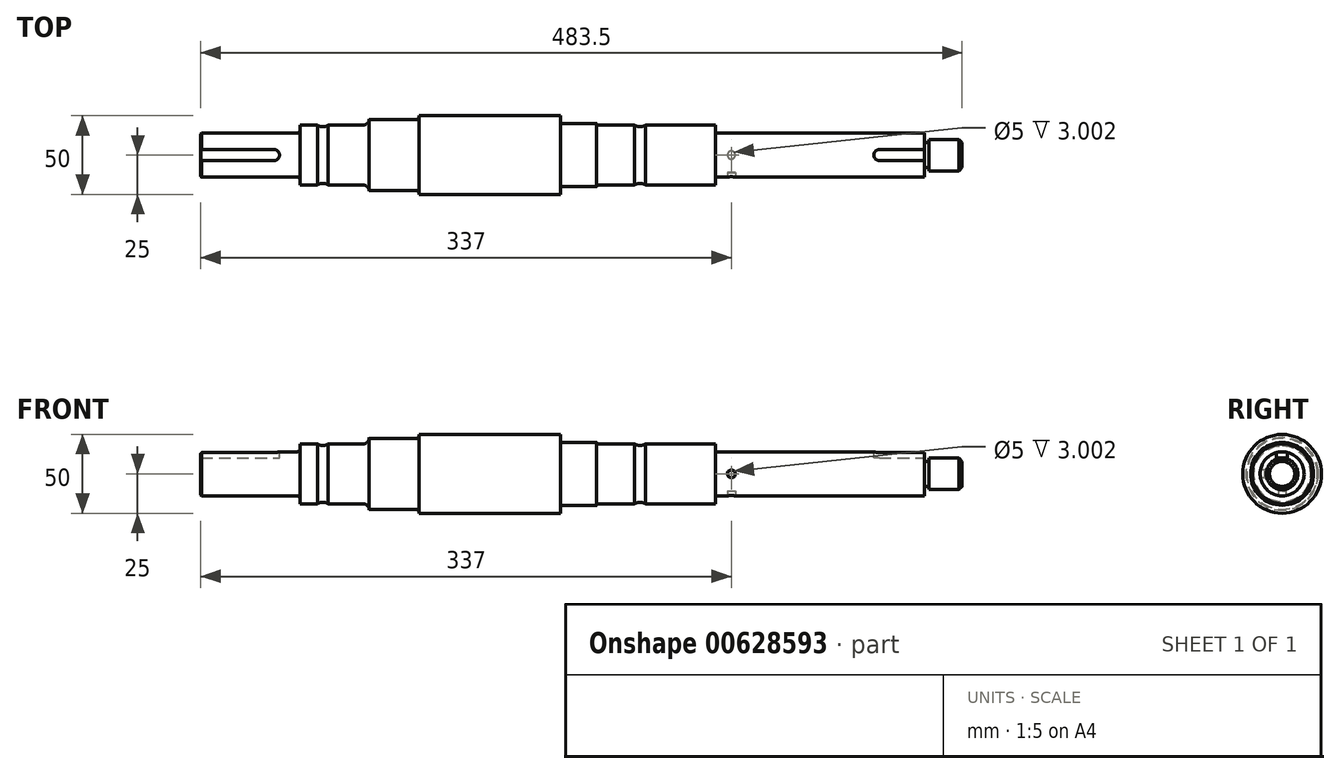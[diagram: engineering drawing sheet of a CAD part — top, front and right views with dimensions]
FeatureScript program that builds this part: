
annotation { "Feature Type Name" : "Feature", "Feature Type Description" : "" }
export const myFeature = defineFeature(function(context is Context, id is Id, definition is map)
    precondition{}
    {
        {
            var Q0;
            Q0=qCreatedBy(makeId("Front.planeOp"),FACE);
            var sketch = newSketch(context, id + "F0", { "sketchPlane" : qUnion([Q0])});
            skLineSegment(sketch, "E0", {"start": v(0, 0) * mm, "end": v(0, 14) * mm});
            skLineSegment(sketch, "E1", {"start": v(0, 14) * mm, "end": v(61, 14) * mm});
            skLineSegment(sketch, "E2", {"start": v(63, 16) * mm, "end": v(63, 19) * mm});
            skLineSegment(sketch, "E3", {"start": v(63, 19) * mm, "end": v(74.1, 19) * mm});
            skArc(sketch, "E4", {"start": v(74.1, 19) * mm, "mid": v(77.5, 18) * mm, "end": v(80.9, 19) * mm});
            skLineSegment(sketch, "E5", {"start": v(80.9, 19) * mm, "end": v(103, 19) * mm});
            skLineSegment(sketch, "E6", {"start": v(107, 22.5) * mm, "end": v(107, 23) * mm});
            skLineSegment(sketch, "E7", {"start": v(107, 22.5) * mm, "end": v(137, 22.5) * mm});
            skLineSegment(sketch, "E8", {"start": v(138.5, 24) * mm, "end": v(138.5, 25) * mm});
            skLineSegment(sketch, "E9", {"start": v(138.5, 25) * mm, "end": v(228.5, 25) * mm});
            skLineSegment(sketch, "E10", {"start": v(228.5, 25) * mm, "end": v(228.5, 21.5) * mm});
            skLineSegment(sketch, "E11", {"start": v(230, 20) * mm, "end": v(251.5, 20) * mm});
            skLineSegment(sketch, "E12", {"start": v(252.91, 19) * mm, "end": v(275.6, 19) * mm});
            skArc(sketch, "E13", {"start": v(275.6, 19) * mm, "mid": v(279, 18) * mm, "end": v(282.4, 19) * mm});
            skLineSegment(sketch, "E14", {"start": v(282.4, 19) * mm, "end": v(327, 19) * mm});
            skLineSegment(sketch, "E15", {"start": v(327, 19) * mm, "end": v(327, 15.5) * mm});
            skLineSegment(sketch, "E16", {"start": v(328.5, 14) * mm, "end": v(459.5, 14) * mm});
            skLineSegment(sketch, "E17", {"start": v(459.5, 14) * mm, "end": v(459.5, 8) * mm});
            skLineSegment(sketch, "E18", {"start": v(459.5, 8) * mm, "end": v(462.5, 8) * mm});
            skLineSegment(sketch, "E19", {"start": v(462.5, 8) * mm, "end": v(462.5, 10) * mm});
            skLineSegment(sketch, "E20", {"start": v(462.5, 10) * mm, "end": v(483.5, 10) * mm});
            skLineSegment(sketch, "E21", {"start": v(483.5, 10) * mm, "end": v(483.5, 0) * mm});
            skLineSegment(sketch, "E22", {"start": v(0, 0) * mm, "end": v(548.97, 0) * mm, "construction": true});
            skPoint(sketch, "E23", {"position": v(77.5, 18) * mm});
            skPoint(sketch, "E24", {"position": v(279, 18) * mm});
            skLineSegment(sketch, "E25", {"start": v(0, 0) * mm, "end": v(483.5, 0) * mm});
            skPoint(sketch, "E26.visualSharp", {"position": v(63, 14) * mm});
            skArc(sketch, "E26.filletArc", {"start": v(61, 14) * mm, "mid": v(62.41, 14.59) * mm, "end": v(63, 16) * mm});
            skPoint(sketch, "E27.visualSharp", {"position": v(107, 19) * mm});
            skArc(sketch, "E27.filletArc", {"start": v(103, 19) * mm, "mid": v(105.83, 20.17) * mm, "end": v(107, 23) * mm});
            skPoint(sketch, "E28.visualSharp", {"position": v(138.5, 22.5) * mm});
            skArc(sketch, "E28.filletArc", {"start": v(137, 22.5) * mm, "mid": v(138.06, 22.94) * mm, "end": v(138.5, 24) * mm});
            skPoint(sketch, "E29.visualSharp", {"position": v(228.5, 20) * mm});
            skArc(sketch, "E29.filletArc", {"start": v(228.5, 21.5) * mm, "mid": v(228.94, 20.44) * mm, "end": v(230, 20) * mm});
            skPoint(sketch, "E30.visualSharp", {"position": v(251.5, 19) * mm});
            skPoint(sketch, "E31.visualSharp", {"position": v(327, 14) * mm});
            skArc(sketch, "E31.filletArc", {"start": v(327, 15.5) * mm, "mid": v(327.44, 14.44) * mm, "end": v(328.5, 14) * mm});
            skArc(sketch, "E32", {"start": v(251.5, 20) * mm, "mid": v(252.05, 19.28) * mm, "end": v(252.91, 19) * mm});
            skSolve(sketch);
        }
        {
            var Q0;
            Q0 = qSketchRegion(id + "F0", true);
            var Q1;
            Q1=sQuery(id+"F0.wireOp",EDGE,"E22");
            revolve(context, id + "F1", {"surfaceOperationType" : NewSurfaceOperationType.NEW, "entities" : qUnion([Q0]), "axis" : qUnion([Q1]), "revolveType" : RevolveType.FULL});
        }
        {
            var Q0;
            Q0=makeQuery(id+"F1.opRevolve","SWEPT_EDGE",EDGE,{"disambiguationData":[OSD([sQuery(id+"F0.wireOp",EDGE,"E0"),sQuery(id+"F0.wireOp",EDGE,"E1")])]});
            chamfer(context, id + "F2", {"entities" : qUnion([Q0]), "chamferType" : ChamferType.OFFSET_ANGLE, "width" : 0.5 * mm, "oppositeDirection" : false, "angle" : 45 * degree, "tangentPropagation" : true});
        }
        {
            var Q0;
            Q0=makeQuery(id+"F1.opRevolve","SWEPT_EDGE",EDGE,{"disambiguationData":[OSD([sQuery(id+"F0.wireOp",EDGE,"E20"),sQuery(id+"F0.wireOp",EDGE,"E21")])]});
            chamfer(context, id + "F3", {"entities" : qUnion([Q0]), "chamferType" : ChamferType.OFFSET_ANGLE, "width" : 2 * mm, "oppositeDirection" : false, "angle" : 45 * degree, "tangentPropagation" : true});
        }
        {
            var Q0;
            Q0=qCreatedBy(makeId("Top.planeOp"),FACE);
            cPlane(context, id + "F4", {"entities" : qUnion([Q0]), "cplaneType" : CPlaneType.OFFSET, "offset" : 14 * mm, "width" : 150 * mm, "height" : 150 * mm});
        }
        {
            var Q0;
            Q0=qCreatedBy(id+"F4.planeOp",FACE);
            var sketch = newSketch(context, id + "F5", { "sketchPlane" : qUnion([Q0])});
            skArc(sketch, "E33", {"start": v(46.5, -3.5) * mm, "mid": v(50, 0) * mm, "end": v(46.5, 3.5) * mm});
            skLineSegment(sketch, "E34", {"start": v(0, 0) * mm, "end": v(53.71, 0) * mm, "construction": true});
            skLineSegment(sketch, "E35.0", {"start": v(0, -3.5) * mm, "end": v(46.5, -3.5) * mm});
            skLineSegment(sketch, "E36.MirrorCS", {"start": v(0, 3.5) * mm, "end": v(46.5, 3.5) * mm});
            skPoint(sketch, "E37", {"position": v(50, 0) * mm});
            skLineSegment(sketch, "E38", {"start": v(0, 3.5) * mm, "end": v(0, -3.5) * mm});
            skSolve(sketch);
        }
        {
            var Q0;
            Q0 = qSketchRegion(id + "F5", true);
            extrude(context, id + "F6", {"entities" : qUnion([Q0]), "operationType" : NewBodyOperationType.REMOVE, "oppositeDirection" : true, "depth" : 4 * mm, "offsetDistance" : 25 * mm});
        }
        {
            var Q0;
            Q0=qCreatedBy(id+"F4.planeOp",FACE);
            var sketch = newSketch(context, id + "F7", { "sketchPlane" : qUnion([Q0])});
            skLineSegment(sketch, "E39", {"start": v(0, 0) * mm, "end": v(507.23, 0) * mm, "construction": true});
            skArc(sketch, "E40", {"start": v(431, 3.5) * mm, "mid": v(427.5, 0) * mm, "end": v(431, -3.5) * mm});
            skLineSegment(sketch, "E41", {"start": v(431, 3.5) * mm, "end": v(459.5, 3.5) * mm});
            skLineSegment(sketch, "E42", {"start": v(431, -3.5) * mm, "end": v(459.5, -3.5) * mm});
            skLineSegment(sketch, "E43.0", {"start": v(459.5, -3.5) * mm, "end": v(459.5, 3.5) * mm});
            skPoint(sketch, "E44.orphan", {"position": v(459.5, 14) * mm});
            skPoint(sketch, "E45.orphan", {"position": v(459.5, -14) * mm});
            skPoint(sketch, "E46", {"position": v(427.5, 0) * mm});
            skSolve(sketch);
        }
        {
            var Q0;
            Q0 = qSketchRegion(id + "F7", true);
            extrude(context, id + "F8", {"entities" : qUnion([Q0]), "operationType" : NewBodyOperationType.REMOVE, "oppositeDirection" : true, "depth" : 4 * mm, "offsetDistance" : 25 * mm});
        }
        {
            var Q0;
            Q0=qCreatedBy(makeId("Front.planeOp"),FACE);
            cPlane(context, id + "F9", {"entities" : qUnion([Q0]), "cplaneType" : CPlaneType.OFFSET, "offset" : 14 * mm, "width" : 150 * mm, "height" : 150 * mm});
        }
        {
            var Q0;
            Q0=qCreatedBy(id+"F9.planeOp",FACE);
            var sketch = newSketch(context, id + "F10", { "sketchPlane" : qUnion([Q0])});
            skLineSegment(sketch, "E47", {"start": v(0, 0) * mm, "end": v(497.27, 0) * mm, "construction": true});
            skCircle(sketch, "E48", {"center": v(337, 0) * mm, "radius": 2.5 * mm});
            skSolve(sketch);
        }
        {
            var Q0;
            Q0 = qSketchRegion(id + "F10", true);
            extrude(context, id + "F11", {"entities" : qUnion([Q0]), "operationType" : NewBodyOperationType.REMOVE, "oppositeDirection" : true, "depth" : 3 * mm, "offsetDistance" : 25 * mm});
        }
        {
            var Q0;
            Q0=qCreatedBy(makeId("Top.planeOp"),FACE);
            cPlane(context, id + "F12", {"entities" : qUnion([Q0]), "cplaneType" : CPlaneType.OFFSET, "offset" : 14 * mm, "oppositeDirection" : true, "width" : 150 * mm, "height" : 150 * mm});
        }
        {
            var Q0;
            Q0=qCreatedBy(id+"F12.planeOp",FACE);
            var sketch = newSketch(context, id + "F13", { "sketchPlane" : qUnion([Q0])});
            skLineSegment(sketch, "E49", {"start": v(0, 0) * mm, "end": v(301.82, 0) * mm, "construction": true});
            skCircle(sketch, "E50", {"center": v(337, 0) * mm, "radius": 2.5 * mm});
            skSolve(sketch);
        }
        {
            var Q0;
            Q0 = qSketchRegion(id + "F13", true);
            extrude(context, id + "F14", {"entities" : qUnion([Q0]), "operationType" : NewBodyOperationType.REMOVE, "depth" : 3 * mm, "offsetDistance" : 25 * mm});
        }
    });
